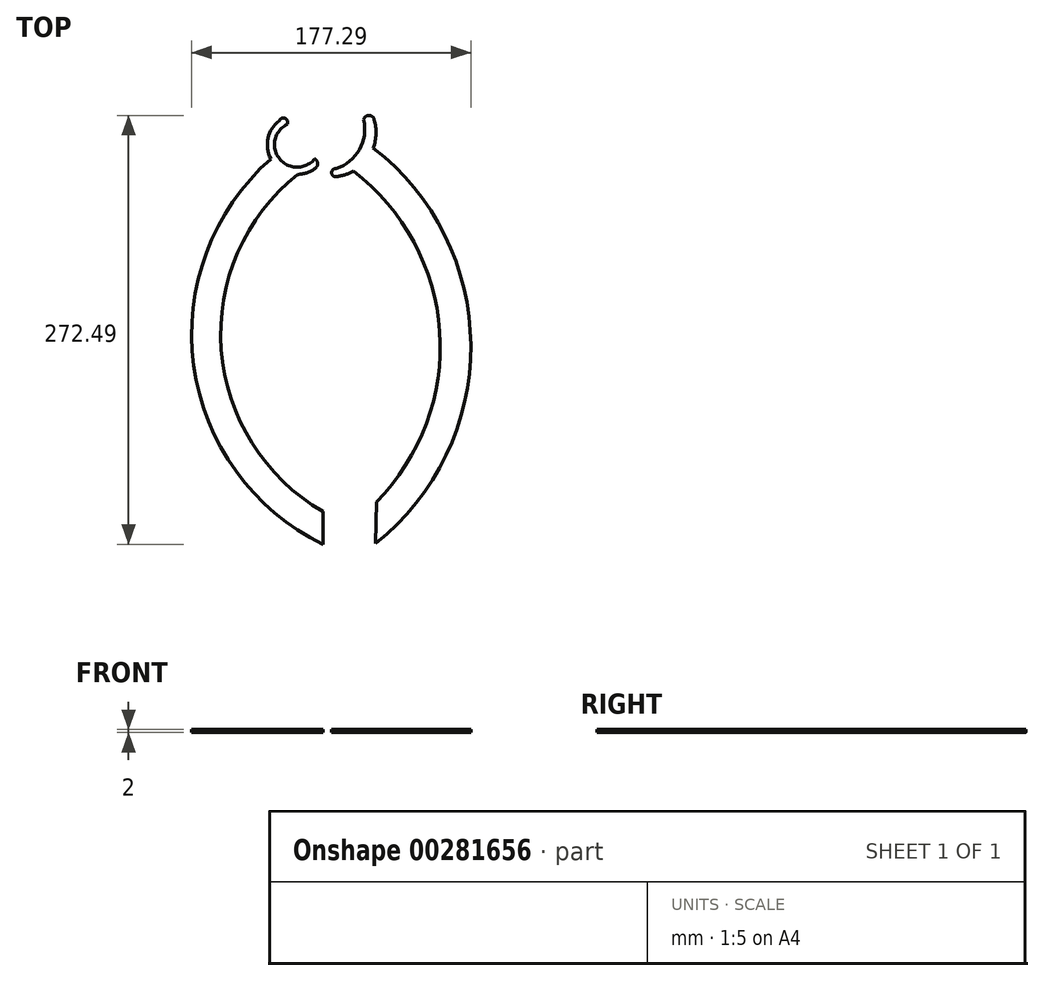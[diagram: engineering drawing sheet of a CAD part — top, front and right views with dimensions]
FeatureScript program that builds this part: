
annotation { "Feature Type Name" : "Feature", "Feature Type Description" : "" }
export const myFeature = defineFeature(function(context is Context, id is Id, definition is map)
    precondition{}
    {
        {
            var Q0;
            Q0=qCreatedBy(makeId("Top.planeOp"),FACE);
            var sketch = newSketch(context, id + "F0", { "sketchPlane" : qUnion([Q0])});
            skArc(sketch, "E0", {"start": v(-17.14, -25.1) * mm, "mid": v(-99.22, 88.49) * mm, "end": v(-50.21, 219.78) * mm});
            skArc(sketch, "E1", {"start": v(-17.14, -4.23) * mm, "mid": v(-81.93, 101.47) * mm, "end": v(-28.7, 213.43) * mm});
            skArc(sketch, "E2", {"start": v(16.38, -24.55) * mm, "mid": v(76.7, 103.46) * mm, "end": v(11.62, 229.12) * mm});
            skArc(sketch, "E3", {"start": v(16.75, 1.8) * mm, "mid": v(56.89, 111.53) * mm, "end": v(0, 213.58) * mm});
            skLineSegment(sketch, "E4", {"start": v(16.75, 1.8) * mm, "end": v(16.38, -24.55) * mm});
            skLineSegment(sketch, "E5", {"start": v(-17.14, -4.23) * mm, "end": v(-17.14, -25.1) * mm});
            skLineSegment(sketch, "E6", {"start": v(-28.48, 213.58) * mm, "end": v(-28.7, 213.43) * mm});
            skPoint(sketch, "E7.endSnap0", {"position": v(8.65, 220.34) * mm});
            skArc(sketch, "E8", {"start": v(-8.25, 208.51) * mm, "mid": v(11.9, 221.09) * mm, "end": v(15.41, 244.57) * mm});
            skArc(sketch, "E9", {"start": v(-8.8, 213.58) * mm, "mid": v(6, 225.65) * mm, "end": v(8.65, 244.57) * mm});
            skArc(sketch, "E10", {"start": v(15.41, 244.57) * mm, "mid": v(12.03, 247.38) * mm, "end": v(8.65, 244.57) * mm});
            skArc(sketch, "E11", {"start": v(-8.8, 213.58) * mm, "mid": v(-11.63, 210.7) * mm, "end": v(-8.25, 208.51) * mm});
            skLineSegment(sketch, "E12", {"start": v(-50.21, 219.78) * mm, "end": v(-50.21, 219.78) * mm});
            skArc(sketch, "E13", {"start": v(-44.86, 244) * mm, "mid": v(-48.79, 217.54) * mm, "end": v(-22.33, 213.58) * mm});
            skArc(sketch, "E14", {"start": v(-39.8, 241.75) * mm, "mid": v(-44.84, 219.9) * mm, "end": v(-22.41, 219.78) * mm});
            skArc(sketch, "E15", {"start": v(-39.8, 241.75) * mm, "mid": v(-41.18, 245.47) * mm, "end": v(-44.86, 244) * mm});
            skArc(sketch, "E16", {"start": v(-22.33, 213.58) * mm, "mid": v(-20.53, 216.7) * mm, "end": v(-22.41, 219.78) * mm});
            skSolve(sketch);
        }
        {
            var Q0;
            Q0 = qSketchRegion(id + "F0", true);
            extrude(context, id + "F1", {"entities" : qUnion([Q0]), "depth" : 2 * mm, "offsetDistance" : 25 * mm});
        }
    });
